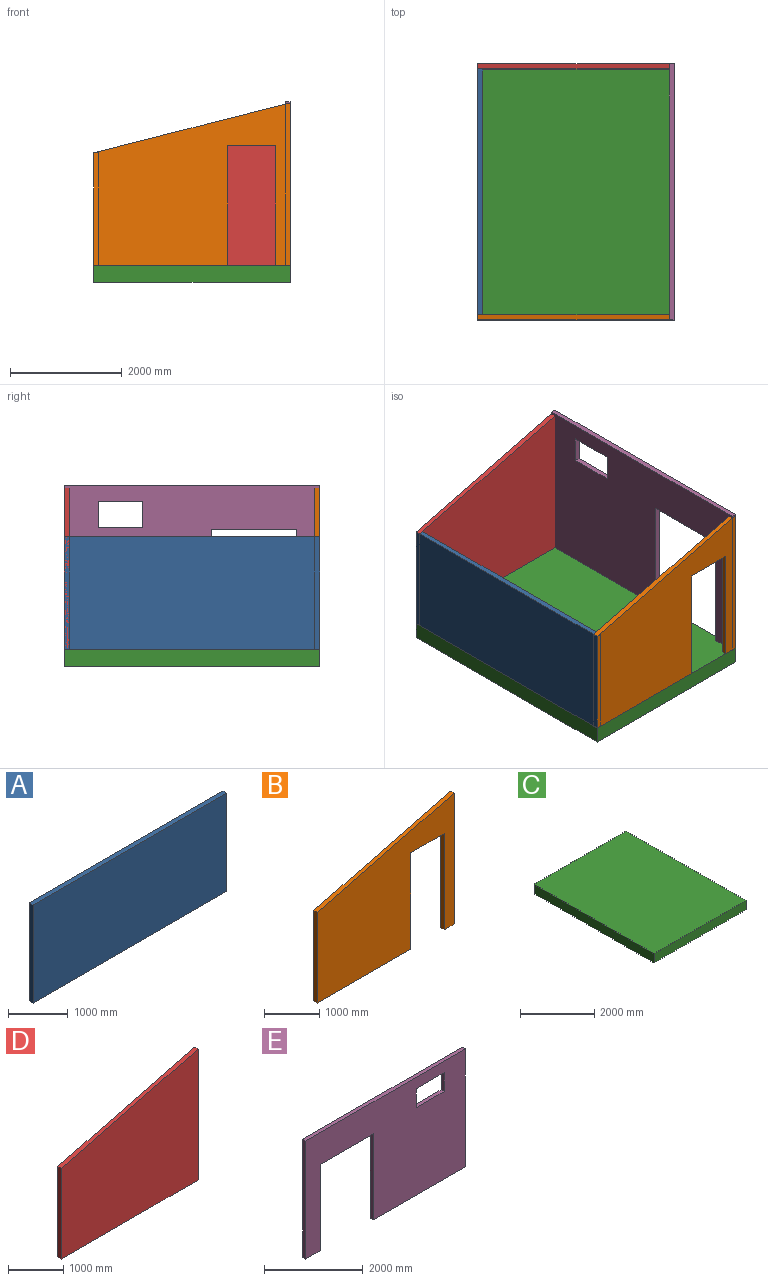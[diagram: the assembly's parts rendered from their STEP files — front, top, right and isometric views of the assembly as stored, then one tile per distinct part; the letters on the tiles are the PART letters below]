
ASSEMBLY  parts=5 mates=6
PART A: 6 faces, bbox 4572x88.9x2006.6 mm
  f0: plane 2006.6x88.9mm, normal (1,0,0), area 178386.9mm2, adj f1,f3,f4,f5
  f1: plane 4572x88.9mm, normal (0,0,1), area 406451.3mm2, adj f0,f2,f4,f5
  f2: plane 2006.6x88.9mm, normal (-1,0,0), area 178386.9mm2, adj f1,f3,f4,f5
  f3: plane 4572x88.9mm, normal (0,0,-1), area 406451.3mm2, adj f0,f2,f4,f5
  f4: plane 4572x2006.6mm, normal (0,-1,0), area 9174175.2mm2, adj f0,f1,f2,f3
  f5: plane 4572x2006.6mm, normal (0,1,0), area 9174175.2mm2, adj f0,f1,f2,f3
PART B: 10 faces, bbox 3505.2x88.9x2902.4 mm
  f0: plane 254x88.9mm, normal (0,0,-1), area 22580.6mm2, adj f1,f2,f4,f7
  f1: plane 3505.2x2902.37mm, normal (0,1,0), area 6760882.6mm2, adj f0,f3,f4,f5,f6,f7,f8,f9
  f2: plane 3505.2x2902.37mm, normal (0,-1,0), area 6760882.6mm2, adj f0,f3,f4,f5,f6,f7,f8,f9
  f3: plane 2387.6x88.9mm, normal (0,0,-1), area 212257.6mm2, adj f1,f2,f6,f8
  f4: plane 2902.37x88.9mm, normal (1,0,0), area 258020.6mm2, adj f0,f1,f2,f5
  f5: plane 3505.2x895.77mm, normal (-0.25,0,0.97), area 321626.8mm2, adj f1,f2,f4,f6
  f6: plane 2006.6x88.9mm, normal (-1,0,0), area 178386.7mm2, adj f1,f2,f3,f5
  f7: plane 2133.6x88.9mm, normal (-1,0,0), area 189677mm2, adj f0,f1,f2,f9
  f8: plane 2133.6x88.9mm, normal (1,0,0), area 189677mm2, adj f1,f2,f3,f9
  f9: plane 863.6x88.9mm, normal (0,0,-1), area 76774mm2, adj f1,f2,f7,f8
PART C: 6 faces, bbox 3505.2x4572x304.8 mm
  f0: plane 3505.2x304.8mm, normal (0,-1,0), area 1068385mm2, adj f1,f3,f4,f5
  f1: plane 4572x304.8mm, normal (1,0,0), area 1393545.6mm2, adj f0,f2,f4,f5
  f2: plane 3505.2x304.8mm, normal (0,1,0), area 1068385mm2, adj f1,f3,f4,f5
  f3: plane 4572x304.8mm, normal (-1,0,0), area 1393545.6mm2, adj f0,f2,f4,f5
  f4: plane 4572x3505.2mm, normal (0,0,1), area 16025774.4mm2, adj f0,f1,f2,f3
  f5: plane 4572x3505.2mm, normal (0,0,-1), area 16025774.4mm2, adj f0,f1,f2,f3
PART D: 6 faces, bbox 3505.2x88.9x2902.4 mm
  f0: plane 3505.2x88.9mm, normal (0,0,-1), area 311612.3mm2, adj f1,f3,f4,f5
  f1: plane 2902.37x88.9mm, normal (1,0,0), area 258020.6mm2, adj f0,f2,f4,f5
  f2: plane 3505.2x895.77mm, normal (-0.25,0,0.97), area 321626.8mm2, adj f1,f3,f4,f5
  f3: plane 2006.6x88.9mm, normal (-1,0,0), area 178386.7mm2, adj f0,f2,f4,f5
  f4: plane 3505.2x2902.37mm, normal (0,1,0), area 8603459.5mm2, adj f0,f1,f2,f3
  f5: plane 3505.2x2902.37mm, normal (0,-1,0), area 8603459.5mm2, adj f0,f1,f2,f3
PART E: 14 faces, bbox 4572x88.9x2921 mm
  f0: plane 469.9x88.9mm, normal (1,0,0), area 41774.2mm2, adj f1,f11,f12,f13
  f1: plane 800.1x88.9mm, normal (0,0,-1), area 71129mm2, adj f0,f2,f12,f13
  f2: plane 469.9x88.9mm, normal (-1,0,0), area 41774.2mm2, adj f1,f11,f12,f13
  f3: plane 414.67x88.9mm, normal (0,0,-1), area 36864mm2, adj f4,f10,f12,f13
  f4: plane 2133.6x88.9mm, normal (1,0,0), area 189677.3mm2, adj f3,f5,f12,f13
  f5: plane 1524x88.9mm, normal (0,0,-1), area 135483.8mm2, adj f4,f6,f12,f13
  f6: plane 2133.6x88.9mm, normal (-1,0,0), area 189677.3mm2, adj f5,f7,f12,f13
  f7: plane 2633.33x88.9mm, normal (0,0,-1), area 234103.6mm2, adj f6,f8,f12,f13
  f8: plane 2921x88.9mm, normal (1,0,0), area 259677.2mm2, adj f7,f9,f12,f13
  f9: plane 4572x88.9mm, normal (0,0,1), area 406451.3mm2, adj f8,f10,f12,f13
  f10: plane 2921x88.9mm, normal (-1,0,0), area 259677.2mm2, adj f3,f9,f12,f13
  f11: plane 800.1x88.9mm, normal (0,0,1), area 71129mm2, adj f0,f2,f12,f13
  f12: plane 4572x2921mm, normal (0,-1,0), area 9727238.6mm2, adj f0,f1,f2,f3,f4,f5,f6,f7
  f13: plane 4572x2921mm, normal (0,1,0), area 9727238.6mm2, adj f0,f1,f2,f3,f4,f5,f6,f7
PLACE A rot(axis=(0,0,1),90deg) t=(-7094.96,4464.59,2035.35)mm
PLACE B t=(-5342.36,66.88,2483.24)mm
PLACE C t=(-5342.36,2352.88,727.25)mm
PLACE D t=(-5342.36,4549.98,2483.24)mm
PLACE E rot(axis=(0,0,1),90deg) t=(-3678.66,6746.95,2492.55)mm
MATE fastened E.f12 <-> C.f1  axis (1,0,0) through (-3589.76,66.88,1032.05)mm
MATE fastened B.f2 <-> E.f10  axis (0,-1,0) through (-3589.76,66.88,1032.05)mm
MATE fastened D.f4 <-> C.f2  axis (0,1,0) through (-7094.96,4638.88,1032.05)mm
MATE fastened A.f5 <-> C.f3  axis (-1,0,0) through (-7094.96,4638.88,1032.05)mm
MATE fastened E.f3 <-> E.f3  axis (0,0,1) through (-3678.66,66.88,1032.05)mm
MATE fastened B.f0 <-> E.f3  axis (0,0,1) through (-3589.76,66.88,1032.05)mm
